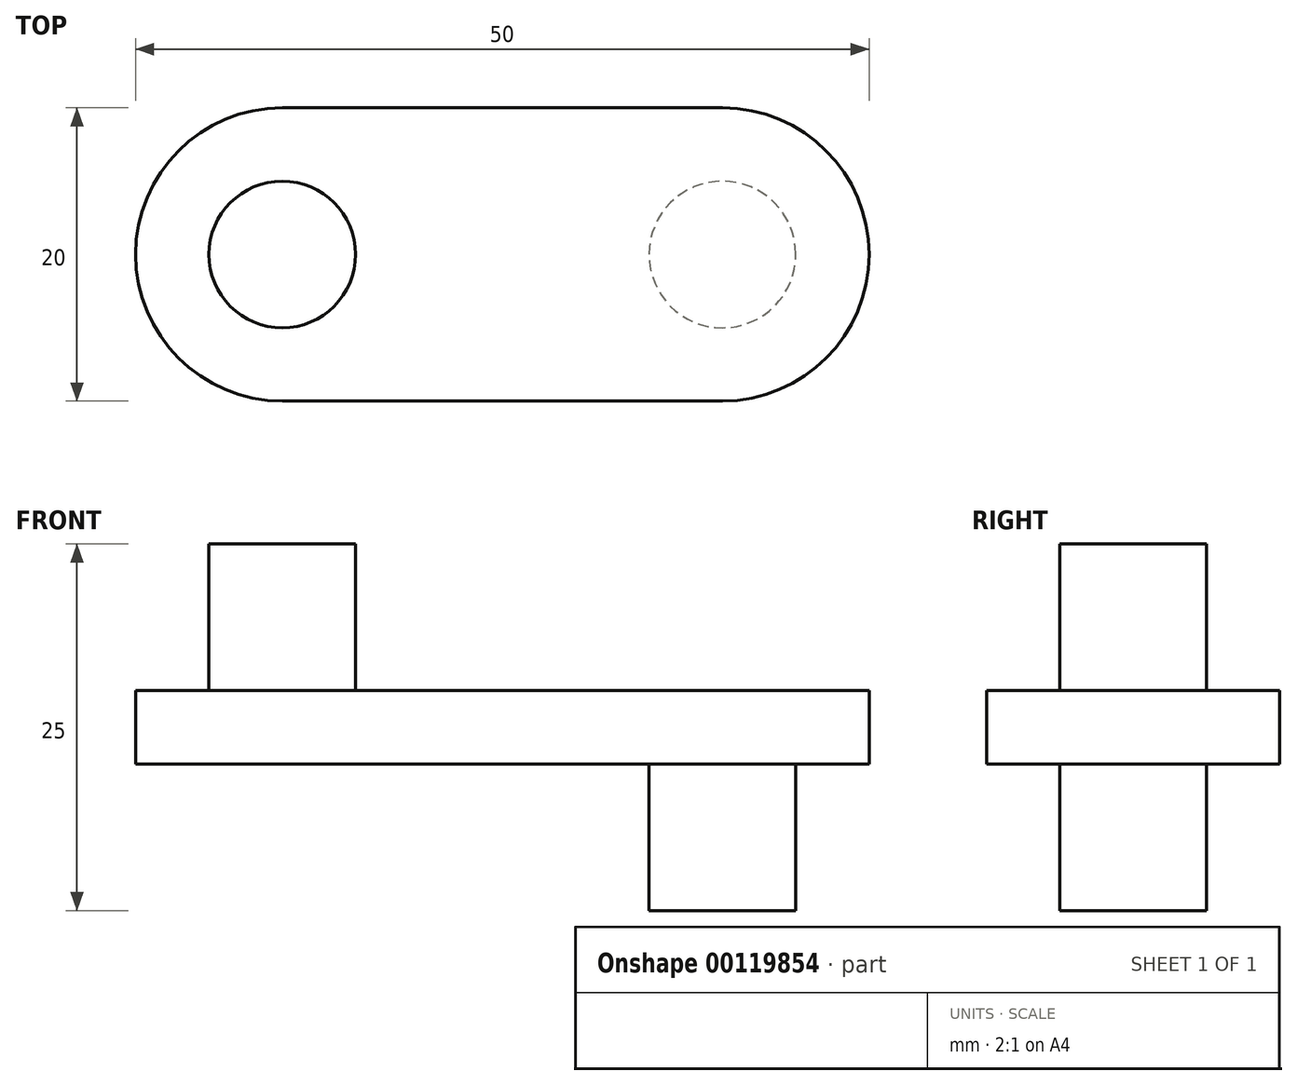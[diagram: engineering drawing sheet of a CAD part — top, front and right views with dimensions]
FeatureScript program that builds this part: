
annotation { "Feature Type Name" : "Feature", "Feature Type Description" : "" }
export const myFeature = defineFeature(function(context is Context, id is Id, definition is map)
    precondition{}
    {
        {
            var Q0;
            Q0=qCreatedBy(makeId("Top.planeOp"),FACE);
            var sketch = newSketch(context, id + "F0", { "sketchPlane" : qUnion([Q0])});
            skLineSegment(sketch, "E0.bottom", {"start": v(0, 0) * mm, "end": v(30, 0) * mm});
            skLineSegment(sketch, "E0.top", {"start": v(0, 20) * mm, "end": v(30, 20) * mm});
            skArc(sketch, "E1", {"start": v(0, 0) * mm, "mid": v(-10, 10) * mm, "end": v(0, 20) * mm});
            skCircle(sketch, "E2", {"center": v(0, 10) * mm, "radius": 5 * mm});
            skArc(sketch, "E3", {"start": v(30, 20) * mm, "mid": v(40, 10) * mm, "end": v(30, 0) * mm});
            skCircle(sketch, "E4", {"center": v(30, 10) * mm, "radius": 5 * mm});
            skSolve(sketch);
        }
        {
            var Q0;
            Q0 = qSketchRegion(id + "F0", true);
            extrude(context, id + "F1", {"entities" : qUnion([Q0]), "depth" : 5 * mm});
        }
        {
            var Q0;
            Q0=qCreatedBy(makeId("Top.planeOp"),FACE);
            var sketch = newSketch(context, id + "F2", { "sketchPlane" : qUnion([Q0])});
            skCircle(sketch, "E5", {"center": v(0, 10) * mm, "radius": 5 * mm});
            skSolve(sketch);
        }
        {
            var Q0;
            Q0 = qSketchRegion(id + "F2", true);
            extrude(context, id + "F3", {"entities" : qUnion([Q0]), "operationType" : NewBodyOperationType.ADD, "depth" : 15 * mm});
        }
        {
            var Q0;
            Q0=qCreatedBy(makeId("Top.planeOp"),FACE);
            var sketch = newSketch(context, id + "F4", { "sketchPlane" : qUnion([Q0])});
            skCircle(sketch, "E6", {"center": v(30, 10) * mm, "radius": 5 * mm});
            skSolve(sketch);
        }
        {
            var Q0;
            Q0 = qSketchRegion(id + "F4", true);
            extrude(context, id + "F5", {"entities" : qUnion([Q0]), "operationType" : NewBodyOperationType.ADD, "oppositeDirection" : true, "depth" : 10 * mm, "hasSecondDirection" : true, "secondDirectionOppositeDirection" : false, "secondDirectionDepth" : 5 * mm});
        }
    });
